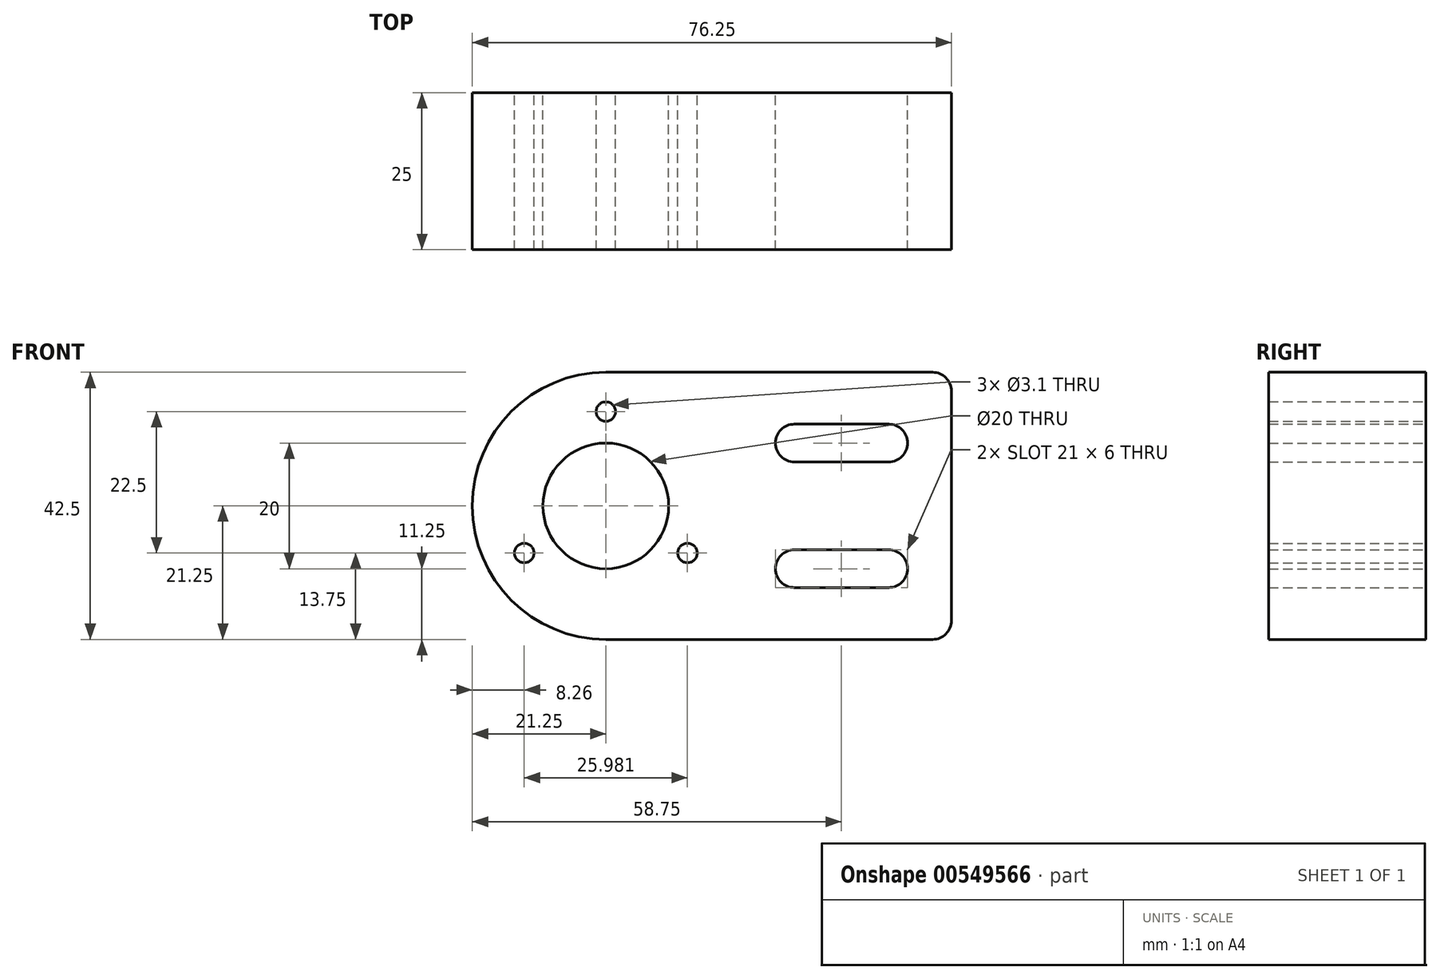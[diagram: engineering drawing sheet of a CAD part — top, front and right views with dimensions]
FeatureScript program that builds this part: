
annotation { "Feature Type Name" : "Feature", "Feature Type Description" : "" }
export const myFeature = defineFeature(function(context is Context, id is Id, definition is map)
    precondition{}
    {
        {
            var Q0;
            Q0=qCreatedBy(makeId("Front.planeOp"),FACE);
            var sketch = newSketch(context, id + "F0", { "sketchPlane" : qUnion([Q0])});
            skCircle(sketch, "E0", {"center": v(0, 0) * mm, "radius": 10 * mm});
            skLineSegment(sketch, "E1.bottom", {"start": v(0, 21.25) * mm, "end": v(52, 21.25) * mm});
            skLineSegment(sketch, "E1.top", {"start": v(0, -21.25) * mm, "end": v(52, -21.25) * mm});
            skLineSegment(sketch, "E1.right", {"start": v(55, 18.25) * mm, "end": v(55, -18.25) * mm});
            skCircle(sketch, "E2", {"center": v(0, 0) * mm, "radius": 21.25 * mm});
            skPoint(sketch, "E3.visualSharp", {"position": v(55, 21.25) * mm});
            skArc(sketch, "E3.filletArc", {"start": v(55, 18.25) * mm, "mid": v(54.12, 20.37) * mm, "end": v(52, 21.25) * mm});
            skPoint(sketch, "E4.visualSharp", {"position": v(55, -21.25) * mm});
            skArc(sketch, "E4.filletArc", {"start": v(52, -21.25) * mm, "mid": v(54.12, -20.37) * mm, "end": v(55, -18.25) * mm});
            skCircle(sketch, "E5", {"center": v(0, 0) * mm, "radius": 15 * mm, "construction": true});
            skCircle(sketch, "E6", {"center": v(0, 15) * mm, "radius": 1.55 * mm});
            skCircle(sketch, "E7.1.0", {"center": v(-13, -7.5) * mm, "radius": 1.55 * mm});
            skCircle(sketch, "E7.2.0", {"center": v(13, -7.5) * mm, "radius": 1.55 * mm});
            skLineSegment(sketch, "E8", {"start": v(30, 10) * mm, "end": v(45, 10) * mm, "construction": true});
            skLineSegment(sketch, "E9", {"start": v(30, -10) * mm, "end": v(45, -10) * mm, "construction": true});
            skLineSegment(sketch, "E10", {"start": v(55, 0) * mm, "end": v(0, 0) * mm, "construction": true});
            skArc(sketch, "E11.0.startCap", {"start": v(30, 7) * mm, "mid": v(27, 10) * mm, "end": v(30, 13) * mm});
            skArc(sketch, "E11.0.endCap", {"start": v(45, 13) * mm, "mid": v(48, 10) * mm, "end": v(45, 7) * mm});
            skLineSegment(sketch, "E11.0.left", {"start": v(30, 13) * mm, "end": v(45, 13) * mm});
            skLineSegment(sketch, "E11.0.right", {"start": v(30, 7) * mm, "end": v(45, 7) * mm});
            skArc(sketch, "E11.1.startCap", {"start": v(30, -13) * mm, "mid": v(27, -10) * mm, "end": v(30, -7) * mm});
            skArc(sketch, "E11.1.endCap", {"start": v(45, -7) * mm, "mid": v(48, -10) * mm, "end": v(45, -13) * mm});
            skLineSegment(sketch, "E11.1.left", {"start": v(30, -7) * mm, "end": v(45, -7) * mm});
            skLineSegment(sketch, "E11.1.right", {"start": v(30, -13) * mm, "end": v(45, -13) * mm});
            skSolve(sketch);
        }
        {
            var Q0;
            Q0 = qSketchRegion(id + "F0", true);
            extrude(context, id + "F1", {"entities" : qUnion([Q0]), "depth" : 25 * mm, "offsetDistance" : 25 * mm});
        }
    });
